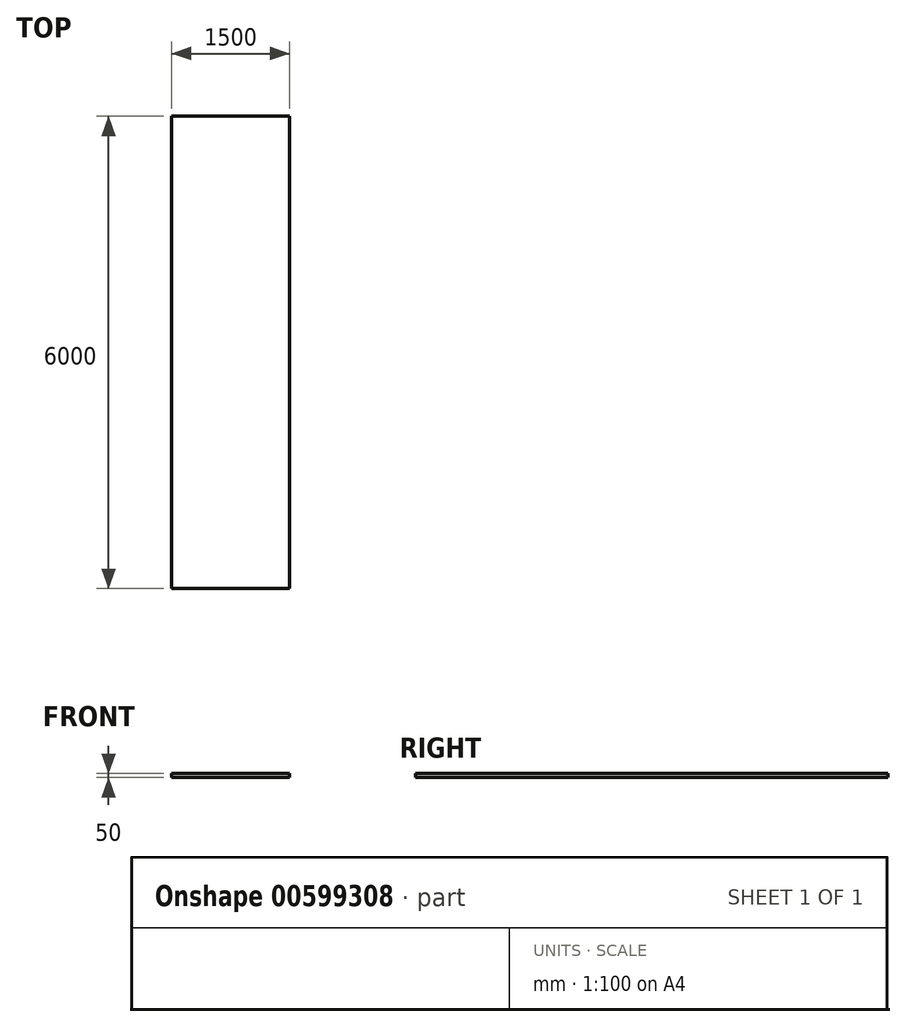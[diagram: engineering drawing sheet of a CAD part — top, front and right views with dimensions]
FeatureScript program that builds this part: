
annotation { "Feature Type Name" : "Feature", "Feature Type Description" : "" }
export const myFeature = defineFeature(function(context is Context, id is Id, definition is map)
    precondition{}
    {
        {
            var Q0;
            Q0=qCreatedBy(makeId("Top.planeOp"),FACE);
            var sketch = newSketch(context, id + "F0", { "sketchPlane" : qUnion([Q0])});
            skLineSegment(sketch, "E0.bottom", {"start": v(-750, 3000) * mm, "end": v(750, 3000) * mm});
            skLineSegment(sketch, "E0.top", {"start": v(-750, -3000) * mm, "end": v(750, -3000) * mm});
            skLineSegment(sketch, "E0.left", {"start": v(-750, 3000) * mm, "end": v(-750, -3000) * mm});
            skLineSegment(sketch, "E0.right", {"start": v(750, 3000) * mm, "end": v(750, -3000) * mm});
            skSolve(sketch);
        }
        {
            var Q0;
            Q0=makeQuery(id+"F0.imprint","IMPRINT",FACE,{"disambiguationData":[TD([[makeQuery(id+"F0.imprint","IMPRINT",EDGE,{"derivedFrom":sQuery(id+"F0.wireOp",EDGE,"E0.bottom")}),-1.0]])]});
            extrude(context, id + "F1", {"entities" : qUnion([Q0]), "depth" : 50 * mm, "offsetDistance" : 25 * mm});
        }
    });
